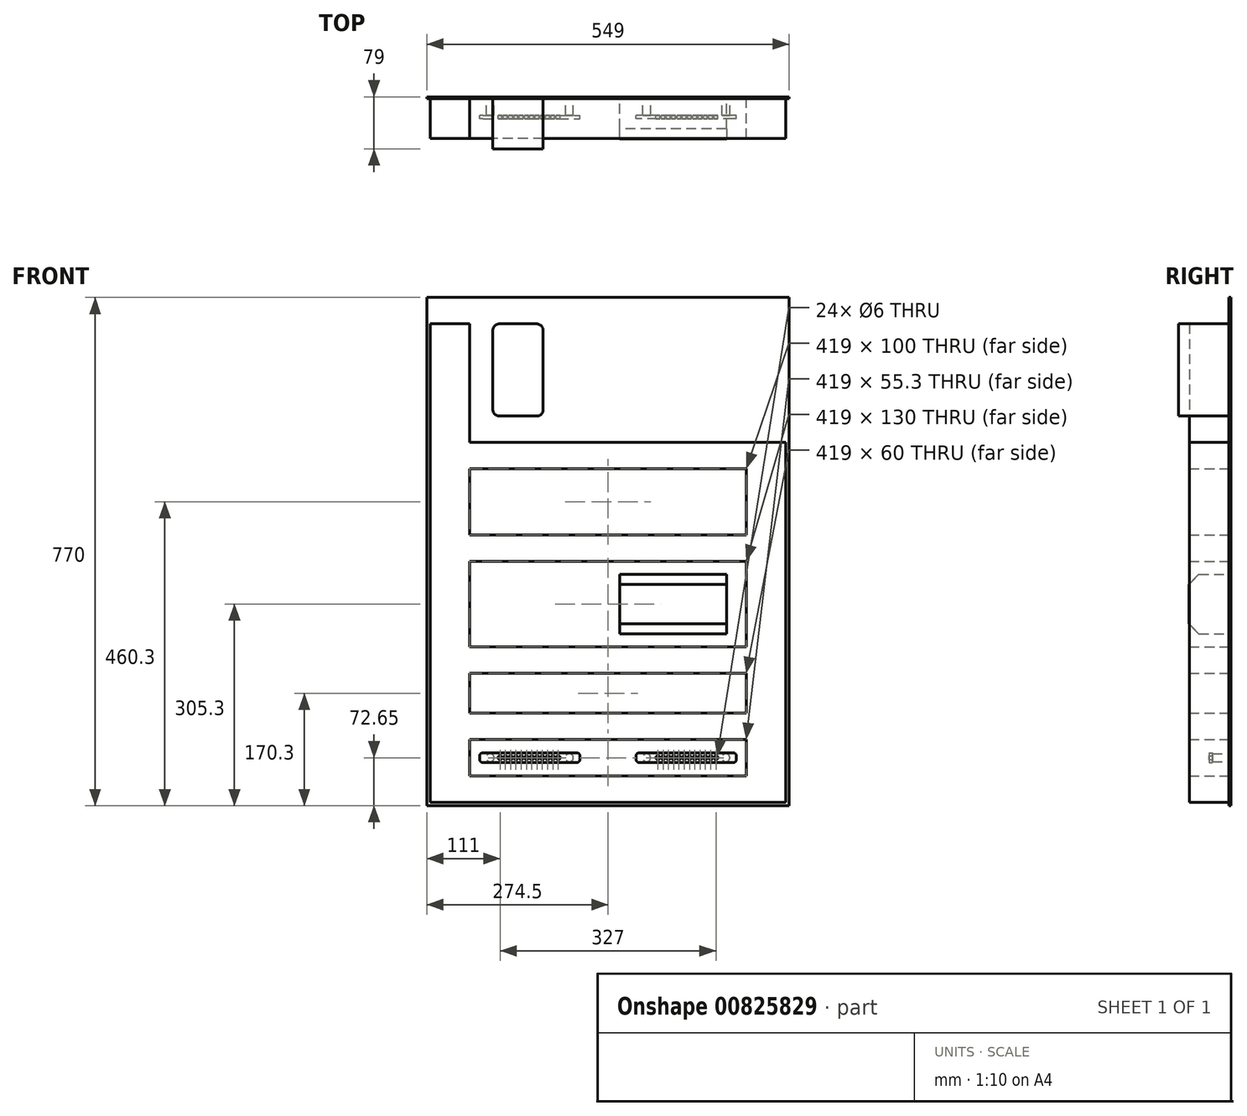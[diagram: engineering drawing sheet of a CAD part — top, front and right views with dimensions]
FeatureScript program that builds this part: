
annotation { "Feature Type Name" : "Feature", "Feature Type Description" : "" }
export const myFeature = defineFeature(function(context is Context, id is Id, definition is map)
    precondition{}
    {
        {
            var Q0;
            Q0=qCreatedBy(makeId("Front.planeOp"),FACE);
            var sketch = newSketch(context, id + "F0", { "sketchPlane" : qUnion([Q0])});
            skLineSegment(sketch, "E0.bottom", {"start": v(274.5, -385) * mm, "end": v(-274.5, -385) * mm});
            skLineSegment(sketch, "E0.top", {"start": v(274.5, 385) * mm, "end": v(-274.5, 385) * mm});
            skLineSegment(sketch, "E0.left", {"start": v(274.5, -385) * mm, "end": v(274.5, 385) * mm});
            skLineSegment(sketch, "E0.right", {"start": v(-274.5, -385) * mm, "end": v(-274.5, 385) * mm});
            skPoint(sketch, "E0.middle", {"position": v(0, 0) * mm});
            skSolve(sketch);
        }
        {
            var Q0;
            Q0 = qSketchRegion(id + "F0", true);
            extrude(context, id + "F1", {"entities" : qUnion([Q0]), "oppositeDirection" : true, "depth" : 3 * mm, "offsetDistance" : 25 * mm});
        }
        {
            var Q0;
            Q0=makeQuery(id+"F1.opExtrude","CAP_FACE",FACE,{"disambiguationData":[OSD([sQuery(id+"F0.wireOp",EDGE,"E0.bottom"),sQuery(id+"F0.wireOp",EDGE,"E0.top"),sQuery(id+"F0.wireOp",EDGE,"E0.left"),sQuery(id+"F0.wireOp",EDGE,"E0.right")])],"isStart":true});
            var sketch = newSketch(context, id + "F2", { "sketchPlane" : qUnion([Q0])});
            skLineSegment(sketch, "E1.bottom", {"start": v(-164.5, 345) * mm, "end": v(-108.3, 345) * mm});
            skLineSegment(sketch, "E1.top", {"start": v(-164.5, 205.3) * mm, "end": v(-108.3, 205.3) * mm});
            skLineSegment(sketch, "E1.left", {"start": v(-174.5, 335) * mm, "end": v(-174.5, 215.3) * mm});
            skLineSegment(sketch, "E1.right", {"start": v(-98.3, 335) * mm, "end": v(-98.3, 215.3) * mm});
            skPoint(sketch, "E2.visualSharp", {"position": v(-174.5, 345) * mm});
            skArc(sketch, "E2.filletArc", {"start": v(-164.5, 345) * mm, "mid": v(-171.57, 342.07) * mm, "end": v(-174.5, 335) * mm});
            skPoint(sketch, "E3.visualSharp", {"position": v(-98.3, 345) * mm});
            skArc(sketch, "E3.filletArc", {"start": v(-98.3, 335) * mm, "mid": v(-101.23, 342.07) * mm, "end": v(-108.3, 345) * mm});
            skPoint(sketch, "E4.visualSharp", {"position": v(-174.5, 205.3) * mm});
            skArc(sketch, "E4.filletArc", {"start": v(-174.5, 215.3) * mm, "mid": v(-171.57, 208.23) * mm, "end": v(-164.5, 205.3) * mm});
            skPoint(sketch, "E5.visualSharp", {"position": v(-98.3, 205.3) * mm});
            skArc(sketch, "E5.filletArc", {"start": v(-108.3, 205.3) * mm, "mid": v(-101.23, 208.23) * mm, "end": v(-98.3, 215.3) * mm});
            skSolve(sketch);
        }
        {
            var Q0;
            Q0 = qSketchRegion(id + "F2", true);
            extrude(context, id + "F3", {"entities" : qUnion([Q0]), "depth" : 76 * mm, "offsetDistance" : 25 * mm});
        }
        {
            var Q0;
            Q0=makeQuery(id+"F1.opExtrude","CAP_FACE",FACE,{"disambiguationData":[OSD([sQuery(id+"F0.wireOp",EDGE,"E0.bottom"),sQuery(id+"F0.wireOp",EDGE,"E0.top"),sQuery(id+"F0.wireOp",EDGE,"E0.left"),sQuery(id+"F0.wireOp",EDGE,"E0.right")])],"isStart":true});
            var sketch = newSketch(context, id + "F4", { "sketchPlane" : qUnion([Q0])});
            skLineSegment(sketch, "E6.bottom", {"start": v(-269.5, 345) * mm, "end": v(-209.5, 345) * mm});
            skLineSegment(sketch, "E6.top", {"start": v(-269.5, -380) * mm, "end": v(-209.5, -380) * mm});
            skLineSegment(sketch, "E6.left", {"start": v(-269.5, 345) * mm, "end": v(-269.5, -380) * mm});
            skLineSegment(sketch, "E6.right", {"start": v(-209.5, 345) * mm, "end": v(-209.5, 25.3) * mm});
            skLineSegment(sketch, "E7.bottom", {"start": v(209.5, 165.3) * mm, "end": v(269.5, 165.3) * mm});
            skLineSegment(sketch, "E7.top", {"start": v(209.5, -380) * mm, "end": v(269.5, -380) * mm});
            skLineSegment(sketch, "E7.left", {"start": v(209.5, 165.3) * mm, "end": v(209.5, 25.3) * mm});
            skLineSegment(sketch, "E7.right", {"start": v(269.5, 165.3) * mm, "end": v(269.5, -380) * mm});
            skLineSegment(sketch, "E8.bottom", {"start": v(-209.5, -340) * mm, "end": v(209.5, -340) * mm});
            skLineSegment(sketch, "E8.top", {"start": v(-209.5, -380) * mm, "end": v(209.5, -380) * mm});
            skLineSegment(sketch, "E8.left", {"start": v(-209.5, -340) * mm, "end": v(-209.5, -380) * mm});
            skLineSegment(sketch, "E8.right", {"start": v(209.5, -340) * mm, "end": v(209.5, -380) * mm});
            skLineSegment(sketch, "E9.bottom", {"start": v(209.5, 165.3) * mm, "end": v(-209.5, 165.3) * mm});
            skLineSegment(sketch, "E9.top", {"start": v(209.5, 125.3) * mm, "end": v(-209.5, 125.3) * mm});
            skLineSegment(sketch, "E9.left", {"start": v(209.5, 165.3) * mm, "end": v(209.5, 125.3) * mm});
            skLineSegment(sketch, "E9.right", {"start": v(-209.5, 165.3) * mm, "end": v(-209.5, 125.3) * mm});
            skLineSegment(sketch, "E10.bottom", {"start": v(-209.5, 25.3) * mm, "end": v(209.5, 25.3) * mm});
            skLineSegment(sketch, "E10.top", {"start": v(-209.5, -14.7) * mm, "end": v(209.5, -14.7) * mm});
            skLineSegment(sketch, "E11.bottom", {"start": v(-209.5, -144.7) * mm, "end": v(209.5, -144.7) * mm});
            skLineSegment(sketch, "E11.top", {"start": v(-209.5, -184.7) * mm, "end": v(209.5, -184.7) * mm});
            skLineSegment(sketch, "E12.bottom", {"start": v(-209.5, -244.7) * mm, "end": v(209.5, -244.7) * mm});
            skLineSegment(sketch, "E12.top", {"start": v(-209.5, -284.7) * mm, "end": v(209.5, -284.7) * mm});
            skLineSegment(sketch, "E13.trimOffspring", {"start": v(-209.5, -14.7) * mm, "end": v(-209.5, -144.7) * mm});
            skLineSegment(sketch, "E14.trimOffspring", {"start": v(209.5, -14.7) * mm, "end": v(209.5, -144.7) * mm});
            skLineSegment(sketch, "E15.trimOffspring", {"start": v(-209.5, -184.7) * mm, "end": v(-209.5, -244.7) * mm});
            skLineSegment(sketch, "E16.trimOffspring", {"start": v(209.5, -184.7) * mm, "end": v(209.5, -244.7) * mm});
            skLineSegment(sketch, "E17.trimOffspring", {"start": v(-209.5, -284.7) * mm, "end": v(-209.5, -380) * mm});
            skLineSegment(sketch, "E18.trimOffspring", {"start": v(209.5, -284.7) * mm, "end": v(209.5, -380) * mm});
            skSolve(sketch);
        }
        {
            var Q0;
            Q0 = qSketchRegion(id + "F4", true);
            extrude(context, id + "F5", {"entities" : qUnion([Q0]), "depth" : 60 * mm, "offsetDistance" : 25 * mm});
        }
        {
            var Q0;
            Q0=makeQuery(id+"F1.opExtrude","CAP_FACE",FACE,{"disambiguationData":[OSD([sQuery(id+"F0.wireOp",EDGE,"E0.bottom"),sQuery(id+"F0.wireOp",EDGE,"E0.top"),sQuery(id+"F0.wireOp",EDGE,"E0.left"),sQuery(id+"F0.wireOp",EDGE,"E0.right")])],"isStart":true});
            var sketch = newSketch(context, id + "F6", { "sketchPlane" : qUnion([Q0])});
            skPoint(sketch, "E19.0", {"position": v(-209.5, -79.7) * mm});
            skPoint(sketch, "E20.0", {"position": v(209.5, -79.7) * mm});
            skLineSegment(sketch, "E21", {"start": v(-209.5, -79.7) * mm, "end": v(209.5, -79.7) * mm, "construction": true});
            skLineSegment(sketch, "E22.bottom", {"start": v(179.5, -124.55) * mm, "end": v(17.8, -124.55) * mm});
            skLineSegment(sketch, "E22.top", {"start": v(179.5, -34.85) * mm, "end": v(17.8, -34.85) * mm});
            skLineSegment(sketch, "E22.left", {"start": v(179.5, -124.55) * mm, "end": v(179.5, -34.85) * mm});
            skLineSegment(sketch, "E22.right", {"start": v(17.8, -124.55) * mm, "end": v(17.8, -34.85) * mm});
            skPoint(sketch, "E22.middle", {"position": v(98.65, -79.7) * mm});
            skSolve(sketch);
        }
        {
            var Q0;
            Q0 = qSketchRegion(id + "F6", true);
            extrude(context, id + "F7", {"entities" : qUnion([Q0]), "depth" : 60.6 * mm, "offsetDistance" : 25 * mm});
        }
        {
            var Q0;
            Q0=makeQuery(id+"F7.opExtrude","CAP_EDGE",EDGE,{"disambiguationData":[OSD([sQuery(id+"F6.wireOp",EDGE,"E22.bottom")])],"isStart":false});
            var Q1;
            Q1=makeQuery(id+"F7.opExtrude","CAP_EDGE",EDGE,{"disambiguationData":[OSD([sQuery(id+"F6.wireOp",EDGE,"E22.top")])],"isStart":false});
            chamfer(context, id + "F8", {"entities" : qUnion([Q0, Q1]), "width" : 15 * mm, "tangentPropagation" : true});
        }
        {
            var Q0;
            Q0=makeQuery(id+"F1.opExtrude","CAP_FACE",FACE,{"disambiguationData":[OSD([sQuery(id+"F0.wireOp",EDGE,"E0.bottom"),sQuery(id+"F0.wireOp",EDGE,"E0.top"),sQuery(id+"F0.wireOp",EDGE,"E0.left"),sQuery(id+"F0.wireOp",EDGE,"E0.right")])],"isStart":true});
            var sketch = newSketch(context, id + "F9", { "sketchPlane" : qUnion([Q0])});
            skPoint(sketch, "E23.0", {"position": v(-209.5, -312.35) * mm});
            skPoint(sketch, "E23.1", {"position": v(209.5, -312.35) * mm});
            skLineSegment(sketch, "E24", {"start": v(-209.5, -312.35) * mm, "end": v(209.5, -312.35) * mm, "construction": true});
            skCircle(sketch, "E25", {"center": v(-178.5, -312.35) * mm, "radius": 6 * mm});
            skCircle(sketch, "E26", {"center": v(-58.5, -312.35) * mm, "radius": 6 * mm});
            skCircle(sketch, "E27.MirrorC", {"center": v(58.5, -312.35) * mm, "radius": 6 * mm});
            skCircle(sketch, "E28.MirrorC", {"center": v(178.5, -312.35) * mm, "radius": 6 * mm});
            skSolve(sketch);
        }
        {
            var Q0;
            Q0 = qSketchRegion(id + "F9", true);
            extrude(context, id + "F10", {"entities" : qUnion([Q0]), "depth" : 25 * mm, "offsetDistance" : 25 * mm});
        }
        {
            var Q0;
            Q0=makeQuery(id+"F10.opExtrude","CAP_FACE",FACE,{"disambiguationData":[OSD([sQuery(id+"F9.wireOp",EDGE,"E25")])],"isStart":false});
            var sketch = newSketch(context, id + "F11", { "sketchPlane" : qUnion([Q0])});
            skLineSegment(sketch, "E29.bottom", {"start": v(-189.5, -304.85) * mm, "end": v(-47.5, -304.85) * mm});
            skLineSegment(sketch, "E29.top", {"start": v(-189.5, -319.85) * mm, "end": v(-47.5, -319.85) * mm});
            skLineSegment(sketch, "E29.left", {"start": v(-194.5, -309.85) * mm, "end": v(-194.5, -314.85) * mm});
            skLineSegment(sketch, "E29.right", {"start": v(-42.5, -309.85) * mm, "end": v(-42.5, -314.85) * mm});
            skPoint(sketch, "E30", {"position": v(-42.5, -312.35) * mm});
            skPoint(sketch, "E31", {"position": v(-178.5, -312.35) * mm});
            skCircle(sketch, "E32", {"center": v(-163.5, -312.35) * mm, "radius": 3 * mm});
            skCircle(sketch, "E33.1.0.0", {"center": v(-155.5, -312.35) * mm, "radius": 3 * mm});
            skCircle(sketch, "E33.2.0.0", {"center": v(-147.5, -312.35) * mm, "radius": 3 * mm});
            skCircle(sketch, "E33.3.0.0", {"center": v(-139.5, -312.35) * mm, "radius": 3 * mm});
            skCircle(sketch, "E33.4.0.0", {"center": v(-131.5, -312.35) * mm, "radius": 3 * mm});
            skCircle(sketch, "E33.5.0.0", {"center": v(-123.5, -312.35) * mm, "radius": 3 * mm});
            skCircle(sketch, "E33.6.0.0", {"center": v(-115.5, -312.35) * mm, "radius": 3 * mm});
            skCircle(sketch, "E33.7.0.0", {"center": v(-107.5, -312.35) * mm, "radius": 3 * mm});
            skCircle(sketch, "E33.8.0.0", {"center": v(-99.5, -312.35) * mm, "radius": 3 * mm});
            skCircle(sketch, "E33.9.0.0", {"center": v(-91.5, -312.35) * mm, "radius": 3 * mm});
            skCircle(sketch, "E33.10.0.0", {"center": v(-83.5, -312.35) * mm, "radius": 3 * mm});
            skCircle(sketch, "E33.11.0.0", {"center": v(-75.5, -312.35) * mm, "radius": 3 * mm});
            skLineSegment(sketch, "E33.direction1", {"start": v(-163.5, -312.35) * mm, "end": v(-155.5, -312.35) * mm, "construction": true});
            skPoint(sketch, "E34.visualSharp", {"position": v(-194.5, -304.85) * mm});
            skArc(sketch, "E34.filletArc", {"start": v(-189.5, -304.85) * mm, "mid": v(-193.04, -306.31) * mm, "end": v(-194.5, -309.85) * mm});
            skPoint(sketch, "E35.visualSharp", {"position": v(-194.5, -319.85) * mm});
            skArc(sketch, "E35.filletArc", {"start": v(-194.5, -314.85) * mm, "mid": v(-193.04, -318.39) * mm, "end": v(-189.5, -319.85) * mm});
            skPoint(sketch, "E36.visualSharp", {"position": v(-42.5, -304.85) * mm});
            skArc(sketch, "E36.filletArc", {"start": v(-42.5, -309.85) * mm, "mid": v(-43.96, -306.31) * mm, "end": v(-47.5, -304.85) * mm});
            skPoint(sketch, "E37.visualSharp", {"position": v(-42.5, -319.85) * mm});
            skArc(sketch, "E37.filletArc", {"start": v(-47.5, -319.85) * mm, "mid": v(-43.96, -318.39) * mm, "end": v(-42.5, -314.85) * mm});
            skArc(sketch, "E38.MirrorCS", {"start": v(-42.5, -314.85) * mm, "mid": v(-43.96, -318.39) * mm, "end": v(-47.5, -319.85) * mm});
            skLineSegment(sketch, "E39.MirrorCS", {"start": v(-42.5, -314.85) * mm, "end": v(-42.5, -309.85) * mm});
            skArc(sketch, "E40.MirrorCS", {"start": v(-47.5, -304.85) * mm, "mid": v(-43.96, -306.31) * mm, "end": v(-42.5, -309.85) * mm});
            skLineSegment(sketch, "E41.MirrorCS", {"start": v(-194.5, -314.85) * mm, "end": v(-194.5, -309.85) * mm});
            skArc(sketch, "E42.MirrorCS", {"start": v(-194.5, -309.85) * mm, "mid": v(-193.04, -306.31) * mm, "end": v(-189.5, -304.85) * mm});
            skArc(sketch, "E43.MirrorCS", {"start": v(-189.5, -319.85) * mm, "mid": v(-193.04, -318.39) * mm, "end": v(-194.5, -314.85) * mm});
            skLineSegment(sketch, "E44.MirrorCS", {"start": v(189.5, -319.85) * mm, "end": v(47.5, -319.85) * mm});
            skLineSegment(sketch, "E45.MirrorCS", {"start": v(189.5, -304.85) * mm, "end": v(47.5, -304.85) * mm});
            skPoint(sketch, "E46.MirrorP", {"position": v(42.5, -319.85) * mm});
            skArc(sketch, "E47.MirrorCS", {"start": v(47.5, -304.85) * mm, "mid": v(43.96, -306.31) * mm, "end": v(42.5, -309.85) * mm});
            skLineSegment(sketch, "E48.MirrorCS", {"start": v(42.5, -309.85) * mm, "end": v(42.5, -314.85) * mm});
            skArc(sketch, "E49.MirrorCS", {"start": v(189.5, -304.85) * mm, "mid": v(193.04, -306.31) * mm, "end": v(194.5, -309.85) * mm});
            skLineSegment(sketch, "E50.MirrorCS", {"start": v(194.5, -309.85) * mm, "end": v(194.5, -314.85) * mm});
            skCircle(sketch, "E51.MirrorC", {"center": v(163.5, -312.35) * mm, "radius": 3 * mm});
            skCircle(sketch, "E52.MirrorC", {"center": v(155.5, -312.35) * mm, "radius": 3 * mm});
            skCircle(sketch, "E53.MirrorC", {"center": v(147.5, -312.35) * mm, "radius": 3 * mm});
            skCircle(sketch, "E54.MirrorC", {"center": v(139.5, -312.35) * mm, "radius": 3 * mm});
            skCircle(sketch, "E55.MirrorC", {"center": v(131.5, -312.35) * mm, "radius": 3 * mm});
            skCircle(sketch, "E56.MirrorC", {"center": v(123.5, -312.35) * mm, "radius": 3 * mm});
            skCircle(sketch, "E57.MirrorC", {"center": v(115.5, -312.35) * mm, "radius": 3 * mm});
            skCircle(sketch, "E58.MirrorC", {"center": v(107.5, -312.35) * mm, "radius": 3 * mm});
            skCircle(sketch, "E59.MirrorC", {"center": v(99.5, -312.35) * mm, "radius": 3 * mm});
            skCircle(sketch, "E60.MirrorC", {"center": v(91.5, -312.35) * mm, "radius": 3 * mm});
            skCircle(sketch, "E61.MirrorC", {"center": v(83.5, -312.35) * mm, "radius": 3 * mm});
            skCircle(sketch, "E62.MirrorC", {"center": v(75.5, -312.35) * mm, "radius": 3 * mm});
            skArc(sketch, "E63.MirrorCS", {"start": v(189.5, -319.85) * mm, "mid": v(193.04, -318.39) * mm, "end": v(194.5, -314.85) * mm});
            skArc(sketch, "E64.MirrorCS", {"start": v(42.5, -314.85) * mm, "mid": v(43.96, -318.39) * mm, "end": v(47.5, -319.85) * mm});
            skSolve(sketch);
        }
        {
            var Q0;
            Q0 = qSketchRegion(id + "F11", true);
            extrude(context, id + "F12", {"entities" : qUnion([Q0]), "depth" : 5 * mm, "offsetDistance" : 25 * mm});
        }
    });
